# Revit family: MTXTYP008
name_source: partatom
category: Furniture
units: mm (PartAtom-declared; Revit-internal decimal feet)

## family parameters
Always vertical = Yes
Cut with Voids When Loaded = No
OmniClass Number = 23.40.20.00
OmniClass Title = General Furniture and Specialties
Render Appearance Source = Family Geometry
Room Calculation Point = No
Shared = No
Work Plane-Based = No

## types (1)
- MTXTYP008
    Cost = 78273 $
    Default Elevation = 0 mm  [stored 0 ft]
    Description = 2 x Devens Black Configurable Task Chair, 4 x Devens Black Configurable Task Chair, 1 x Spin Out Pencil Drawer Radius, 1 x Side Access Rollout Tower Hanging Folder Rail Painted, 1 x Metal Landscape Paper Tray Painted, 1 x BOX / FILE PEDESTAL MOBILE w/CUSHION 12"W, 1 x 69 in. Electrical Jumper  (Pt 48E), 8 x Matrix Black Duplex Outlet - Line 1, 4 x 18 in. Electrical Jumper  (Panel To Panel), 3 x 21 in. Electrical Jumper  (Extended Panel To Panel), 8 x Single Powerway Assembly - 36W - 8 wire, 4 circuit, 1 x Single Powerway Assembly - 48W - 8 wire, 4 circuit, 4 x Access Hole Cover, 1 x LH Receptacle Mounted Base Infeed - 72L - 8 Wire, 4 Circuit, 2 x Universal 8 Wire 4 Cir I Connector, 2 x 24 in. Electrical Jumper  (Vt 24), 1 x Volker Cube w/Casters - 18x18x18, 3 x Dual Electrical Tile - 8H X 36W, 6 x Dual Electrical Tile - 8H X 36W, 1 x Dual Electrical Tile - 8H X 48W, 1 x MX Monolithic Laminate Tile Single Sided 48H X 30W, 1 x Steel Tile - 8H x 48W, 7 x Tackable Acoustical Tile - 16H x 36W, 6 x Tackable Acoustical Tile - 24H x 36W, 1 x Tackable Acoustical Tile - 24H x 48W, 1 x Tackable Acoustical Tile - 32H x 36W, 1 x Tackable Acoustical Tile - 32H x 48W, 4 x Tackable Acoustical Tile - 40H x 36W, 2 x Tackable Acoustical Tile - 40H x 48W, 1 x Tackable Acoustical Tile - 48H x 30W, 4 x Tackable Acoustical Tile - 48H x 36W, 1 x White Board Tile - 24H x 36W, 2 x 3-Way  90 Degree Connector - Linear Trim - 50H, 1 x 2-Way 90 Degree Connector - Linear Trim - 50H, 2 x Frame End Cap - Linear Trim - 50H, 2 x Panel Frame - Linear Trim - 42H x 36W, 2 x Panel Frame - Linear Trim - 42H x 48W, 1 x Panel Frame - Linear Trim - 50H x 30W, 6 x Panel Frame - Linear Trim - 50H x 36W, 1 x GALLERY PANEL-END OF RUN SINGLE FOR WING-50H X 72W LH HORZ, 1 x MTX Gallery Panel EOR Single-50H x 24W LH Vert, 1 x MTX Gallery Panel EOR Single-50H x 24W RH Vert, 1 x MATRIX GALLERY PANEL WING LH 50H X 30W HORZ GRAIN, 4 x Connector HiLo - Linear Trim -  8H, 1 x Utility Tool Tile - Linear Trim - 8H x 48W, 1 x WESKO FILE BAR - 12", 1 x Cushion for Credenza - 18D x 36W, 1 x Wardrobe Tower Right Lseries B/B/F W/Side Bookshelf 49"H, 1 x REF: W-WS1848; TO BE 50"W TO ALIGN WITH 22"D WKSF; Worksurface Rect 18"D X 50"W X 1 1/8"Th, 1 x REF: W-WS2448; TO BE 22"D APROX. TO MATCH L SERIES STORAGE; Rectangular - 2mm Edge - 224D x 48W, 1 x Day to Day HA 3-leg WS SQ Edge 30d x 72w x 24d x 42w Right, 1 x TBL, REC, 2mm, 24Dx72Wx29H, HAL, GLD, 1 x TBL, RND, 2mm, 30Dx29H, DISC, GLD, 2 x Calibrate HAT Single Foot Kit 24" V2, 1 x Rectangular - 2mm Edge - 24D x 56W, 1 x Rectangular - 2mm Edge - 24D x 72W, 1 x Rectangular - 2mm Edge - 24D x 78W, 1 x N-Leg 2.5 x 2.5 Post 27H 24D, 6 x Flat Plate, 5 x Regular Cantilever - Left Hand - 24D, 5 x Regular Cantilever - Right Hand - 24D, 1 x CBX HA E 2-Leg base with WS SQ Edge 24d x 72w, 4 x Bar Pull Handle with Paint Options, 2 x CBX Combo B/F Ped Left/Bookcase Right 18D x 21H x 60W, 1 x CBX Combo B/F Ped Right/Bookcase Left 18D x 21H x 48W, 1 x Cbx 2d Full Depth Cab 18dx21hx36w, 1 x CBX Side Access Roll Out Tower RH 24Dx50Hx15W, 1 x Channel Scrn,Panel Top,GL250,Dim A,SMnt,Uni,12hx72w, 1 x Channel Scrn,Panel Top,GL250,Dim A,SMnt,Uni,12hx84w, 1 x Lite Clip Scrn,Terri Drp,PET,Dim A,UMnt,LH,20hx24w, 1 x Channel Scrn,GP Side,PET,Dim R,SMnt,Uni,50hx24w, 1 x Lite Clip Scrn,LWrp PM,PET,Dim J,UMnt,LH,26hx24dx36w
    Exported From CET Designer = Yes
    Manufacturer = AIS
    Model = 4600C
    Show MTXTYP008 = Yes
    VisibilityIndex = 0

note: [stored X ft] marks values corroborated as IEEE doubles in the binary element streams (Revit-internal decimal feet)

## geometry (parser evidence)
native form markers: Sweep x2
no freeform markers — native parametric forms only
